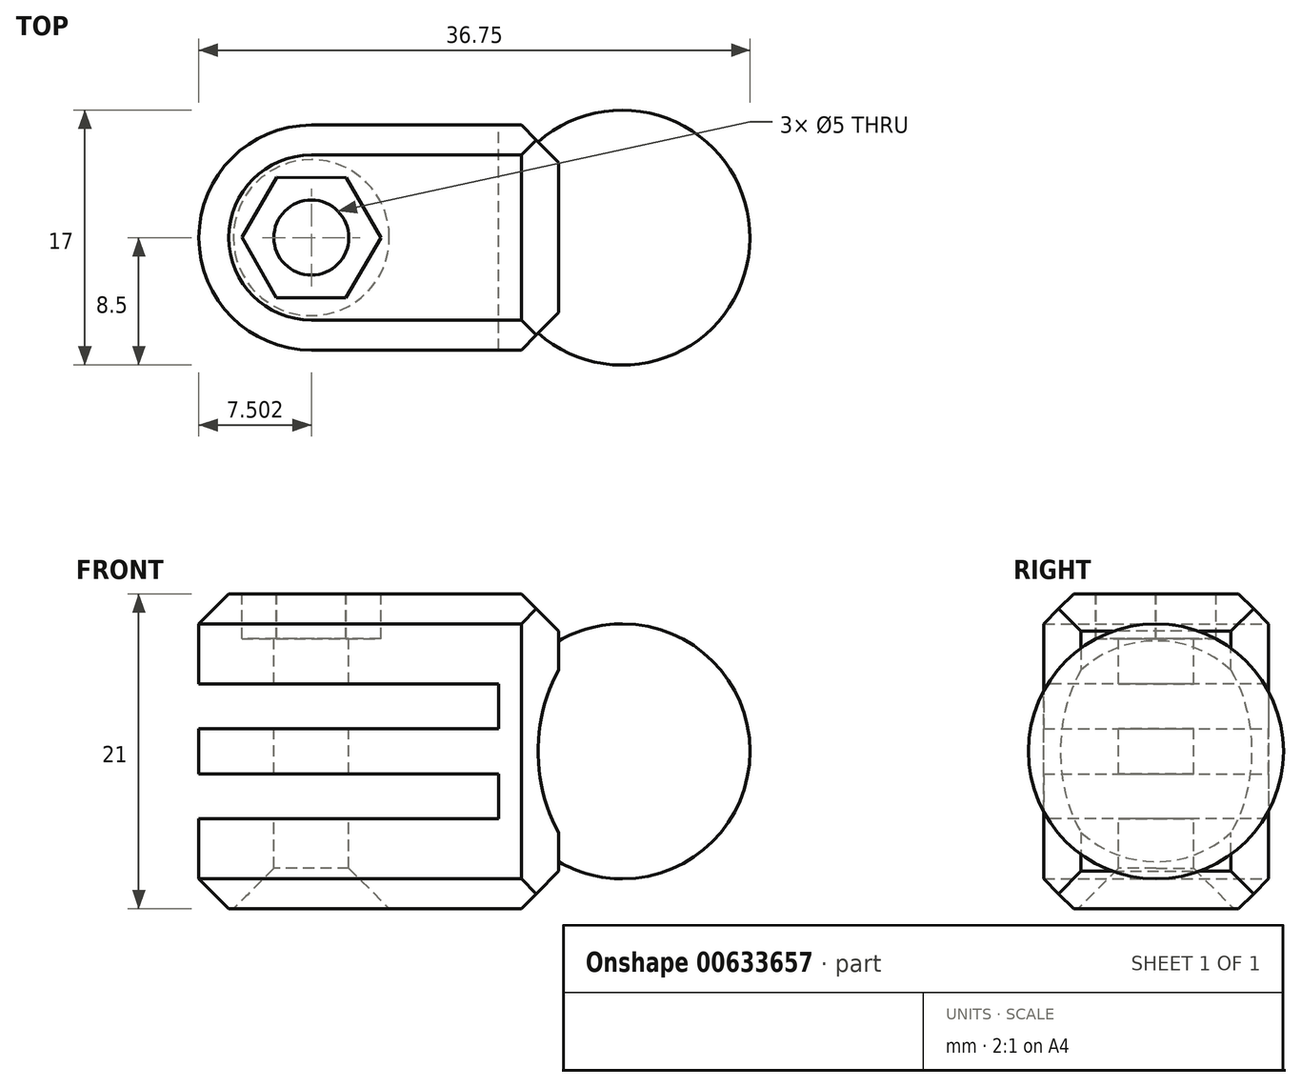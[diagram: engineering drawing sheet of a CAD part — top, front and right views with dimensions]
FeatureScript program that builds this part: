
annotation { "Feature Type Name" : "Feature", "Feature Type Description" : "" }
export const myFeature = defineFeature(function(context is Context, id is Id, definition is map)
    precondition{}
    {
        {
            var Q0;
            Q0=qCreatedBy(makeId("Front.planeOp"),FACE);
            var sketch = newSketch(context, id + "F0", { "sketchPlane" : qUnion([Q0])});
            skArc(sketch, "E0", {"start": v(0, 8.5) * mm, "mid": v(-8.5, 0) * mm, "end": v(0, -8.5) * mm});
            skLineSegment(sketch, "E1", {"start": v(0, 8.5) * mm, "end": v(0, -8.5) * mm});
            skSolve(sketch);
        }
        {
            var Q0;
            Q0=makeQuery(id+"F0.imprint","IMPRINT",FACE,{"disambiguationData":[TD([[makeQuery(id+"F0.imprint","IMPRINT",EDGE,{"derivedFrom":sQuery(id+"F0.wireOp",EDGE,"E0")}),1.0]])]});
            var Q1;
            Q1=sQuery(id+"F0.wireOp",EDGE,"E1");
            revolve(context, id + "F1", {"entities" : qUnion([Q0]), "axis" : qUnion([Q1]), "revolveType" : RevolveType.FULL});
        }
        {
            var Q0;
            Q0=qCreatedBy(makeId("Front.planeOp"),FACE);
            var sketch = newSketch(context, id + "F2", { "sketchPlane" : qUnion([Q0])});
            skLineSegment(sketch, "E2.bottom", {"start": v(-8.75, 7.5) * mm, "end": v(-4.25, 7.5) * mm});
            skLineSegment(sketch, "E2.top", {"start": v(-8.75, -7.5) * mm, "end": v(-4.25, -7.5) * mm});
            skLineSegment(sketch, "E2.left", {"start": v(-8.75, 7.5) * mm, "end": v(-8.75, -7.5) * mm});
            skLineSegment(sketch, "E2.right", {"start": v(-4.25, 7.5) * mm, "end": v(-4.25, -7.5) * mm});
            skPoint(sketch, "E2.middle", {"position": v(-6.5, 0) * mm});
            skSolve(sketch);
        }
        {
            var Q0;
            Q0=makeQuery(id+"F2.imprint","IMPRINT",FACE,{"disambiguationData":[TD([[makeQuery(id+"F2.imprint","IMPRINT",EDGE,{"derivedFrom":sQuery(id+"F2.wireOp",EDGE,"E2.bottom")}),-1.0]])]});
            extrude(context, id + "F3", {"entities" : qUnion([Q0]), "operationType" : NewBodyOperationType.REMOVE, "oppositeDirection" : true, "depth" : 25 * mm, "offsetDistance" : 25 * mm, "symmetric" : true});
        }
        {
            var Q0;
            Q0=makeQuery(id+"F3.boolean.opBoolean","COPY",FACE,{"derivedFrom":makeQuery(id+"F3.opExtrude","SWEPT_FACE",FACE,{"disambiguationData":[OSD([sQuery(id+"F2.wireOp",EDGE,"E2.right")])]})});
            var sketch = newSketch(context, id + "F4", { "sketchPlane" : qUnion([Q0])});
            skLineSegment(sketch, "E3.bottom", {"start": v(7.5, 10.5) * mm, "end": v(-7.5, 10.5) * mm});
            skLineSegment(sketch, "E3.top", {"start": v(7.5, -10.5) * mm, "end": v(-7.5, -10.5) * mm});
            skLineSegment(sketch, "E3.left", {"start": v(7.5, 10.5) * mm, "end": v(7.5, -10.5) * mm});
            skLineSegment(sketch, "E3.right", {"start": v(-7.5, 10.5) * mm, "end": v(-7.5, -10.5) * mm});
            skPoint(sketch, "E3.middle", {"position": v(0, 0) * mm});
            skSolve(sketch);
        }
        {
            var Q0;
            Q0 = qSketchRegion(id + "F4", true);
            extrude(context, id + "F5", {"entities" : qUnion([Q0]), "operationType" : NewBodyOperationType.ADD, "depth" : 4 * mm, "offsetDistance" : 25 * mm});
        }
        {
            var Q0;
            Q0=makeQuery(id+"F5.opExtrude","CAP_FACE",FACE,{"disambiguationData":[OSD([sQuery(id+"F4.wireOp",EDGE,"E3.bottom"),sQuery(id+"F4.wireOp",EDGE,"E3.top"),sQuery(id+"F4.wireOp",EDGE,"E3.left"),sQuery(id+"F4.wireOp",EDGE,"E3.right")])],"isStart":false});
            var sketch = newSketch(context, id + "F6", { "sketchPlane" : qUnion([Q0])});
            skLineSegment(sketch, "E4.bottom", {"start": v(7.5, 1.5) * mm, "end": v(-7.5, 1.5) * mm});
            skLineSegment(sketch, "E4.top", {"start": v(7.5, -1.5) * mm, "end": v(-7.5, -1.5) * mm});
            skLineSegment(sketch, "E4.left", {"start": v(7.5, 1.5) * mm, "end": v(7.5, -1.5) * mm});
            skLineSegment(sketch, "E4.right", {"start": v(-7.5, 1.5) * mm, "end": v(-7.5, -1.5) * mm});
            skPoint(sketch, "E4.middle", {"position": v(0, 0) * mm});
            skLineSegment(sketch, "E5", {"start": v(-7.5, 1.5) * mm, "end": v(-7.5, 4.5) * mm, "construction": true});
            skLineSegment(sketch, "E6", {"start": v(-7.5, -1.5) * mm, "end": v(-7.5, -4.5) * mm, "construction": true});
            skLineSegment(sketch, "E7.bottom", {"start": v(-7.5, 4.5) * mm, "end": v(7.5, 4.5) * mm});
            skLineSegment(sketch, "E7.top", {"start": v(-7.5, 10.5) * mm, "end": v(7.5, 10.5) * mm});
            skLineSegment(sketch, "E7.left", {"start": v(-7.5, 4.5) * mm, "end": v(-7.5, 10.5) * mm});
            skLineSegment(sketch, "E7.right", {"start": v(7.5, 4.5) * mm, "end": v(7.5, 10.5) * mm});
            skLineSegment(sketch, "E8.bottom", {"start": v(-7.5, -4.5) * mm, "end": v(7.5, -4.5) * mm});
            skLineSegment(sketch, "E8.top", {"start": v(-7.5, -10.5) * mm, "end": v(7.5, -10.5) * mm});
            skLineSegment(sketch, "E8.left", {"start": v(-7.5, -4.5) * mm, "end": v(-7.5, -10.5) * mm});
            skLineSegment(sketch, "E8.right", {"start": v(7.5, -4.5) * mm, "end": v(7.5, -10.5) * mm});
            skSolve(sketch);
        }
        {
            var Q0;
            Q0=makeQuery(id+"F6.imprint","IMPRINT",FACE,{"disambiguationData":[TD([[makeQuery(id+"F6.imprint","IMPRINT",EDGE,{"derivedFrom":sQuery(id+"F6.wireOp",EDGE,"E8.bottom")}),-1.0]])]});
            var Q1;
            Q1=makeQuery(id+"F6.imprint","IMPRINT",FACE,{"disambiguationData":[TD([[makeQuery(id+"F6.imprint","IMPRINT",EDGE,{"derivedFrom":sQuery(id+"F6.wireOp",EDGE,"E4.bottom")}),1.0]])]});
            var Q2;
            Q2=makeQuery(id+"F6.imprint","IMPRINT",FACE,{"disambiguationData":[TD([[makeQuery(id+"F6.imprint","IMPRINT",EDGE,{"derivedFrom":sQuery(id+"F6.wireOp",EDGE,"E7.bottom")}),1.0]])]});
            extrude(context, id + "F7", {"entities" : qUnion([Q0, Q1, Q2]), "operationType" : NewBodyOperationType.ADD, "depth" : 20 * mm, "offsetDistance" : 25 * mm});
        }
        {
            var Q0;
            Q0=makeQuery(id+"F7.boolean.opBoolean","MERGE",FACE,{"derivedFrom":[makeQuery(id+"F5.opExtrude","SWEPT_FACE",FACE,{"disambiguationData":[OSD([sQuery(id+"F4.wireOp",EDGE,"E3.bottom")])]}),makeQuery(id+"F7.opExtrude","SWEPT_FACE",FACE,{"disambiguationData":[OSD([sQuery(id+"F6.wireOp",EDGE,"E7.top")])]})]});
            var sketch = newSketch(context, id + "F8", { "sketchPlane" : qUnion([Q0])});
            skLineSegment(sketch, "E9", {"start": v(-28.25, 0) * mm, "end": v(-20.75, 0) * mm, "construction": true});
            skPoint(sketch, "E9.endSnap0", {"position": v(-28.25, 0) * mm});
            skCircle(sketch, "E10", {"center": v(-20.75, 0) * mm, "radius": 7.5 * mm});
            skCircle(sketch, "E11", {"center": v(-20.75, 0) * mm, "radius": 2.5 * mm});
            skCircle(sketch, "E12.cCircle", {"center": v(-20.75, 0) * mm, "radius": 4.01 * mm, "construction": true});
            skLineSegment(sketch, "E12.0", {"start": v(-23.08, -4) * mm, "end": v(-25.38, 0.02) * mm});
            skLineSegment(sketch, "E12.1", {"start": v(-25.38, 0.02) * mm, "end": v(-23.04, 4.02) * mm});
            skLineSegment(sketch, "E12.2", {"start": v(-23.04, 4.02) * mm, "end": v(-18.41, 4) * mm});
            skLineSegment(sketch, "E12.3", {"start": v(-18.41, 4) * mm, "end": v(-16.12, -0.02) * mm});
            skLineSegment(sketch, "E12.4", {"start": v(-16.12, -0.02) * mm, "end": v(-18.45, -4.02) * mm});
            skLineSegment(sketch, "E12.5", {"start": v(-18.45, -4.02) * mm, "end": v(-23.08, -4) * mm});
            skPoint(sketch, "E12.0.midPoint", {"position": v(-24.23, -1.99) * mm});
            skLineSegment(sketch, "E13", {"start": v(-20.75, 0) * mm, "end": v(-24.23, -1.99) * mm, "construction": true});
            skSolve(sketch);
        }
        {
            var Q0;
            {var subQ0=sQuery(id+"F8.wireOp",EDGE,"E10");var subQ1=sQuery(id+"F6.wireOp",EDGE,"E7.top");var subQ2=makeQuery(id+"F7.opExtrude","CAP_EDGE",EDGE,{"disambiguationData":[OSD([subQ1])],"isStart":false});var subQ3=makeQuery(id+"F8.imprint","INTERSECT",VERTEX,{"derivedFrom":[subQ2,subQ0]});Q0=makeQuery(id+"F8.imprint","IMPRINT",FACE,{"disambiguationData":[TD([[makeQuery(id+"F8.imprint","IMPRINT",EDGE,{"disambiguationData":[TD([[subQ3,-1.0]])],"derivedFrom":subQ0}),-1.0]])]});}
            var Q1;
            {var subQ0=sQuery(id+"F8.wireOp",EDGE,"E10");var subQ1=sQuery(id+"F6.wireOp",EDGE,"E7.top");var subQ2=makeQuery(id+"F7.opExtrude","CAP_EDGE",EDGE,{"disambiguationData":[OSD([subQ1])],"isStart":false});var subQ3=makeQuery(id+"F8.imprint","INTERSECT",VERTEX,{"derivedFrom":[subQ2,subQ0]});Q1=makeQuery(id+"F8.imprint","IMPRINT",FACE,{"disambiguationData":[TD([[makeQuery(id+"F8.imprint","IMPRINT",EDGE,{"disambiguationData":[TD([[subQ3,1.0]])],"derivedFrom":subQ0}),-1.0]])]});}
            var Q2;
            Q2=makeQuery(id+"F8.imprint","IMPRINT",FACE,{"disambiguationData":[TD([[makeQuery(id+"F8.imprint","IMPRINT",EDGE,{"derivedFrom":sQuery(id+"F8.wireOp",EDGE,"E11")}),1.0]])]});
            extrude(context, id + "F9", {"entities" : qUnion([Q0, Q1, Q2]), "operationType" : NewBodyOperationType.REMOVE, "oppositeDirection" : true, "depth" : 25 * mm, "offsetDistance" : 25 * mm});
        }
        {
            var Q0;
            Q0=makeQuery(id+"F5.opExtrude","CAP_EDGE",EDGE,{"disambiguationData":[OSD([sQuery(id+"F4.wireOp",EDGE,"E3.left")])],"isStart":true});
            var Q1;
            Q1=makeQuery(id+"F5.opExtrude","CAP_EDGE",EDGE,{"disambiguationData":[OSD([sQuery(id+"F4.wireOp",EDGE,"E3.bottom")])],"isStart":true});
            var Q2;
            Q2=makeQuery(id+"F5.opExtrude","CAP_EDGE",EDGE,{"disambiguationData":[OSD([sQuery(id+"F4.wireOp",EDGE,"E3.top")])],"isStart":true});
            var Q3;
            Q3=makeQuery(id+"F5.opExtrude","CAP_EDGE",EDGE,{"disambiguationData":[OSD([sQuery(id+"F4.wireOp",EDGE,"E3.right")])],"isStart":true});
            chamfer(context, id + "F10", {"entities" : qUnion([Q0, Q1, Q2, Q3]), "width" : 2.5 * mm, "tangentPropagation" : true});
        }
        {
            var Q0;
            Q0=makeQuery(id+"F7.boolean.opBoolean","MERGE",EDGE,{"derivedFrom":[makeQuery(id+"F5.opExtrude","SWEPT_EDGE",EDGE,{"disambiguationData":[OSD([sQuery(id+"F4.wireOp",EDGE,"E3.bottom"),sQuery(id+"F4.wireOp",EDGE,"E3.left")])]}),makeQuery(id+"F7.opExtrude","SWEPT_EDGE",EDGE,{"disambiguationData":[OSD([sQuery(id+"F6.wireOp",EDGE,"E7.top"),sQuery(id+"F6.wireOp",EDGE,"E7.right")])]})]});
            var Q1;
            Q1=makeQuery(id+"F7.boolean.opBoolean","MERGE",EDGE,{"derivedFrom":[makeQuery(id+"F5.opExtrude","SWEPT_EDGE",EDGE,{"disambiguationData":[OSD([sQuery(id+"F4.wireOp",EDGE,"E3.top"),sQuery(id+"F4.wireOp",EDGE,"E3.left")])]}),makeQuery(id+"F7.opExtrude","SWEPT_EDGE",EDGE,{"disambiguationData":[OSD([sQuery(id+"F6.wireOp",EDGE,"E8.top"),sQuery(id+"F6.wireOp",EDGE,"E8.right")])]})]});
            chamfer(context, id + "F11", {"entities" : qUnion([Q0, Q1]), "width" : 2 * mm, "tangentPropagation" : true});
        }
        {
            var Q0;
            Q0=makeQuery(id+"F8.imprint","IMPRINT",FACE,{"disambiguationData":[TD([[makeQuery(id+"F8.imprint","IMPRINT",EDGE,{"derivedFrom":sQuery(id+"F8.wireOp",EDGE,"E11")}),-1.0]])]});
            extrude(context, id + "F12", {"entities" : qUnion([Q0]), "operationType" : NewBodyOperationType.REMOVE, "oppositeDirection" : true, "depth" : 3 * mm, "offsetDistance" : 25 * mm});
        }
        {
            var Q0;
            Q0=makeQuery(id+"F9.boolean.opBoolean","INTERSECT",EDGE,{"derivedFrom":[makeQuery(id+"F7.boolean.opBoolean","MERGE",FACE,{"derivedFrom":[makeQuery(id+"F5.opExtrude","SWEPT_FACE",FACE,{"disambiguationData":[OSD([sQuery(id+"F4.wireOp",EDGE,"E3.top")])]}),makeQuery(id+"F7.opExtrude","SWEPT_FACE",FACE,{"disambiguationData":[OSD([sQuery(id+"F6.wireOp",EDGE,"E8.top")])]})]}),makeQuery(id+"F9.opExtrude","SWEPT_FACE",FACE,{"disambiguationData":[OSD([sQuery(id+"F8.wireOp",EDGE,"E11")])]})]});
            chamfer(context, id + "F13", {"entities" : qUnion([Q0]), "width" : 2.7 * mm, "tangentPropagation" : true});
        }
    });
